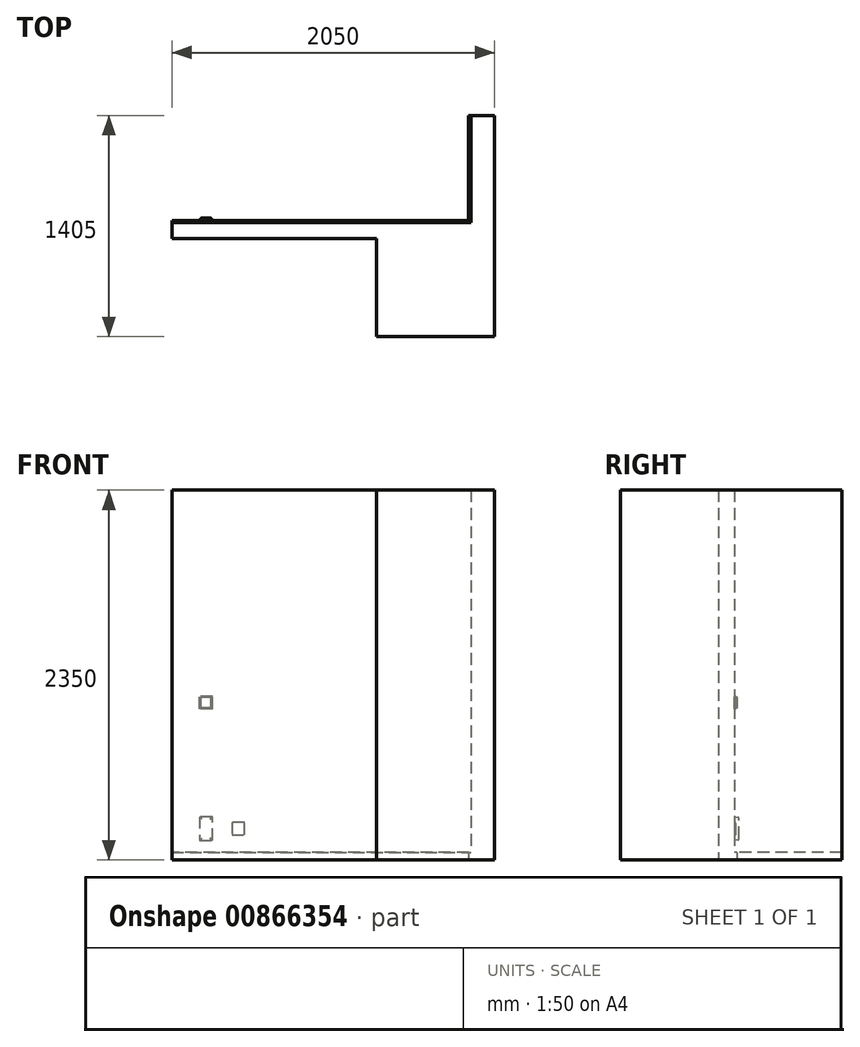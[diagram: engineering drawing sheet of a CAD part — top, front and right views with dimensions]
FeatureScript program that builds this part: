
annotation { "Feature Type Name" : "Feature", "Feature Type Description" : "" }
export const myFeature = defineFeature(function(context is Context, id is Id, definition is map)
    precondition{}
    {
        {
            var Q0;
            Q0=qCreatedBy(makeId("Top.planeOp"),FACE);
            var sketch = newSketch(context, id + "F0", { "sketchPlane" : qUnion([Q0])});
            skLineSegment(sketch, "E0", {"start": v(-339.73, 55.95) * mm, "end": v(1560.27, 55.95) * mm});
            skLineSegment(sketch, "E1", {"start": v(1560.27, 55.95) * mm, "end": v(1560.27, 55.95) * mm});
            skLineSegment(sketch, "E2", {"start": v(1560.27, 55.95) * mm, "end": v(1560.27, 737.95) * mm});
            skLineSegment(sketch, "E3", {"start": v(1560.27, 737.95) * mm, "end": v(1710.27, 737.95) * mm});
            skLineSegment(sketch, "E4", {"start": v(1710.27, 737.95) * mm, "end": v(1710.27, -667.05) * mm});
            skLineSegment(sketch, "E5", {"start": v(1710.27, -667.05) * mm, "end": v(960.27, -667.05) * mm});
            skLineSegment(sketch, "E6", {"start": v(960.27, -667.05) * mm, "end": v(960.27, -44.71) * mm});
            skLineSegment(sketch, "E7", {"start": v(960.27, -44.71) * mm, "end": v(-339.73, -44.71) * mm});
            skLineSegment(sketch, "E8", {"start": v(-339.73, -44.71) * mm, "end": v(-339.73, 55.95) * mm});
            skLineSegment(sketch, "E9.bottom", {"start": v(-214.73, 55.95) * mm, "end": v(-134.73, 55.95) * mm});
            skLineSegment(sketch, "E9.top", {"start": v(-214.73, 75.95) * mm, "end": v(-134.73, 75.95) * mm});
            skLineSegment(sketch, "E9.left", {"start": v(-214.73, 55.95) * mm, "end": v(-214.73, 75.95) * mm});
            skLineSegment(sketch, "E9.right", {"start": v(-134.73, 55.95) * mm, "end": v(-134.73, 75.95) * mm});
            skSolve(sketch);
        }
        {
            var Q0;
            Q0=makeQuery(id+"F0.imprint","IMPRINT",FACE,{"disambiguationData":[TD([[makeQuery(id+"F0.imprint","IMPRINT",EDGE,{"derivedFrom":sQuery(id+"F0.wireOp",EDGE,"E0")}),-1.0]])]});
            extrude(context, id + "F1", {"entities" : qUnion([Q0]), "depth" : 2350 * mm, "offsetDistance" : 25 * mm});
        }
        {
            var Q0;
            Q0=makeQuery(id+"F1.opExtrude","SWEPT_FACE",FACE,{"disambiguationData":[OSD([sQuery(id+"F0.wireOp",EDGE,"E2")])]});
            var sketch = newSketch(context, id + "F2", { "sketchPlane" : qUnion([Q0])});
            skLineSegment(sketch, "E10", {"start": v(-737.95, 50) * mm, "end": v(-55.95, 50) * mm});
            skSolve(sketch);
        }
        {
            var Q0;
            Q0=makeQuery(id+"F1.opExtrude","SWEPT_FACE",FACE,{"disambiguationData":[OSD([sQuery(id+"F0.wireOp",EDGE,"E0"),sQuery(id+"F0.wireOp",EDGE,"E9.bottom")])]});
            var sketch = newSketch(context, id + "F3", { "sketchPlane" : qUnion([Q0])});
            skLineSegment(sketch, "E11", {"start": v(-1560.27, 50) * mm, "end": v(339.73, 50) * mm});
            skSolve(sketch);
        }
        {
            var Q0;
            {var subQ0=sQuery(id+"F2.wireOp",EDGE,"E10");Q0=makeQuery(id+"F2.imprint","IMPRINT",FACE,{"disambiguationData":[TD([[makeQuery(id+"F2.imprint","IMPRINT",EDGE,{"derivedFrom":subQ0}),-1.0]])]});}
            extrude(context, id + "F4", {"entities" : qUnion([Q0]), "operationType" : NewBodyOperationType.ADD, "depth" : 15 * mm, "offsetDistance" : 25 * mm});
        }
        {
            var Q0;
            {var subQ0=sQuery(id+"F3.wireOp",EDGE,"E11");Q0=makeQuery(id+"F3.imprint","IMPRINT",FACE,{"disambiguationData":[TD([[makeQuery(id+"F3.imprint","IMPRINT",EDGE,{"derivedFrom":subQ0}),-1.0]])]});}
            extrude(context, id + "F5", {"entities" : qUnion([Q0]), "operationType" : NewBodyOperationType.ADD, "depth" : 15 * mm, "offsetDistance" : 25 * mm});
        }
        {
            var Q0;
            Q0=makeQuery(id+"F1.opExtrude","SWEPT_FACE",FACE,{"disambiguationData":[OSD([sQuery(id+"F0.wireOp",EDGE,"E0"),sQuery(id+"F0.wireOp",EDGE,"E9.bottom")])]});
            var sketch = newSketch(context, id + "F6", { "sketchPlane" : qUnion([Q0])});
            skLineSegment(sketch, "E12.bottom", {"start": v(82.36, 960) * mm, "end": v(162.36, 960) * mm});
            skLineSegment(sketch, "E12.top", {"start": v(82.36, 1040) * mm, "end": v(162.36, 1040) * mm});
            skLineSegment(sketch, "E12.left", {"start": v(82.36, 960) * mm, "end": v(82.36, 1040) * mm});
            skLineSegment(sketch, "E12.right", {"start": v(162.36, 960) * mm, "end": v(162.36, 1040) * mm});
            skPoint(sketch, "E12.middle", {"position": v(122.36, 1000) * mm});
            skLineSegment(sketch, "E13.bottom", {"start": v(162.36, 275) * mm, "end": v(82.36, 275) * mm});
            skLineSegment(sketch, "E13.top", {"start": v(162.36, 125) * mm, "end": v(82.36, 125) * mm});
            skLineSegment(sketch, "E13.left", {"start": v(162.36, 275) * mm, "end": v(162.36, 125) * mm});
            skLineSegment(sketch, "E13.right", {"start": v(82.36, 275) * mm, "end": v(82.36, 125) * mm});
            skPoint(sketch, "E13.middle", {"position": v(122.36, 200) * mm});
            skPoint(sketch, "E13.middle.positionSnap0", {"position": v(122.36, 960) * mm});
            skPoint(sketch, "E13.centerSnap0", {"position": v(122.36, 960) * mm});
            skLineSegment(sketch, "E14.bottom", {"start": v(-122.03, 240) * mm, "end": v(-42.03, 240) * mm});
            skLineSegment(sketch, "E14.top", {"start": v(-122.03, 160) * mm, "end": v(-42.03, 160) * mm});
            skLineSegment(sketch, "E14.left", {"start": v(-122.03, 240) * mm, "end": v(-122.03, 160) * mm});
            skLineSegment(sketch, "E14.right", {"start": v(-42.03, 240) * mm, "end": v(-42.03, 160) * mm});
            skPoint(sketch, "E14.middle", {"position": v(-82.03, 200) * mm});
            skSolve(sketch);
        }
        {
            var Q0;
            Q0=makeQuery(id+"F6.imprint","IMPRINT",FACE,{"disambiguationData":[TD([[makeQuery(id+"F6.imprint","IMPRINT",EDGE,{"derivedFrom":sQuery(id+"F6.wireOp",EDGE,"E12.bottom")}),1.0]])]});
            extrude(context, id + "F7", {"entities" : qUnion([Q0]), "operationType" : NewBodyOperationType.ADD, "depth" : 10 * mm, "offsetDistance" : 25 * mm});
        }
        {
            var Q0;
            Q0=makeQuery(id+"F7.opExtrude","CAP_FACE",FACE,{"disambiguationData":[OSD([sQuery(id+"F6.wireOp",EDGE,"E12.bottom"),sQuery(id+"F6.wireOp",EDGE,"E12.top"),sQuery(id+"F6.wireOp",EDGE,"E12.left"),sQuery(id+"F6.wireOp",EDGE,"E12.right")])],"isStart":false});
            var sketch = newSketch(context, id + "F8", { "sketchPlane" : qUnion([Q0])});
            skLineSegment(sketch, "E15.0", {"start": v(89.36, 1033) * mm, "end": v(155.36, 1033) * mm});
            skLineSegment(sketch, "E15.1", {"start": v(89.36, 967) * mm, "end": v(89.36, 1033) * mm});
            skLineSegment(sketch, "E15.2", {"start": v(89.36, 967) * mm, "end": v(155.36, 967) * mm});
            skLineSegment(sketch, "E15.3", {"start": v(155.36, 967) * mm, "end": v(155.36, 1033) * mm});
            skSolve(sketch);
        }
        {
            var Q0;
            Q0=makeQuery(id+"F8.imprint","IMPRINT",FACE,{"disambiguationData":[TD([[makeQuery(id+"F8.imprint","IMPRINT",EDGE,{"derivedFrom":sQuery(id+"F8.wireOp",EDGE,"E15.0")}),-1.0]])]});
            extrude(context, id + "F9", {"entities" : qUnion([Q0]), "operationType" : NewBodyOperationType.ADD, "depth" : 10 * mm, "offsetDistance" : 25 * mm});
        }
        {
            var Q0;
            Q0=makeQuery(id+"F6.imprint","IMPRINT",FACE,{"disambiguationData":[TD([[makeQuery(id+"F6.imprint","IMPRINT",EDGE,{"derivedFrom":sQuery(id+"F6.wireOp",EDGE,"E13.bottom")}),1.0]])]});
            extrude(context, id + "F10", {"entities" : qUnion([Q0]), "operationType" : NewBodyOperationType.ADD, "depth" : 30 * mm, "offsetDistance" : 25 * mm, "hasDraft" : true, "draftAngle" : 10 * degree, "draftPullDirection" : true});
        }
        {
            var Q0;
            Q0=makeQuery(id+"F10.opExtrude","CAP_FACE",FACE,{"disambiguationData":[OSD([sQuery(id+"F6.wireOp",EDGE,"E13.bottom"),sQuery(id+"F6.wireOp",EDGE,"E13.top"),sQuery(id+"F6.wireOp",EDGE,"E13.left"),sQuery(id+"F6.wireOp",EDGE,"E13.right")])],"isStart":false});
            fillet(context, id + "F11", {"entities" : qUnion([Q0]), "radius" : 10 * mm, "tangentPropagation" : true, "allowEdgeOverflow" : false});
        }
        {
            var Q0;
            Q0=makeQuery(id+"F6.imprint","IMPRINT",FACE,{"disambiguationData":[TD([[makeQuery(id+"F6.imprint","IMPRINT",EDGE,{"derivedFrom":sQuery(id+"F6.wireOp",EDGE,"E14.bottom")}),-1.0]])]});
            extrude(context, id + "F12", {"entities" : qUnion([Q0]), "operationType" : NewBodyOperationType.ADD, "depth" : 10 * mm, "offsetDistance" : 25 * mm, "hasDraft" : true, "draftAngle" : 3 * degree});
        }
    });
